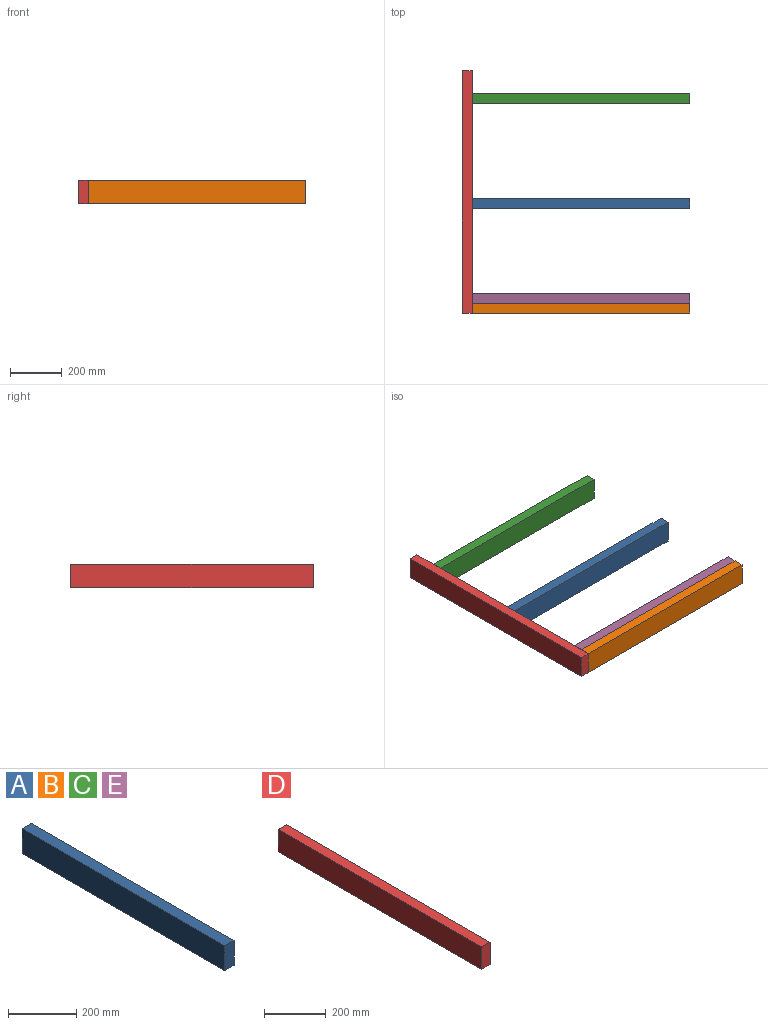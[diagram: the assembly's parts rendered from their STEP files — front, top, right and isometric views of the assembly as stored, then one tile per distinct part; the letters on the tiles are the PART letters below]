
ASSEMBLY  parts=5 mates=1
PART A: 6 faces, bbox 38.1x838.2x88.9 mm
  f0: plane 838.2x38.1mm, normal (0,0,-1), area 31935.4mm2, adj f1,f3,f4,f5
  f1: plane 838.2x88.9mm, normal (1,0,0), area 74516mm2, adj f0,f2,f4,f5
  f2: plane 838.2x38.1mm, normal (0,0,1), area 31935.4mm2, adj f1,f3,f4,f5
  f3: plane 838.2x88.9mm, normal (-1,0,0), area 74516mm2, adj f0,f2,f4,f5
  f4: plane 88.9x38.1mm, normal (0,-1,0), area 3387.1mm2, adj f0,f1,f2,f3
  f5: plane 88.9x38.1mm, normal (0,1,0), area 3387.1mm2, adj f0,f1,f2,f3
PART B: same geometry as A
PART C: same geometry as A
PART D: 6 faces, bbox 38.1x933.5x88.9 mm
  f0: plane 933.45x38.1mm, normal (0,0,-1), area 35564.4mm2, adj f1,f3,f4,f5
  f1: plane 933.45x88.9mm, normal (1,0,0), area 82983.7mm2, adj f0,f2,f4,f5
  f2: plane 933.45x38.1mm, normal (0,0,1), area 35564.4mm2, adj f1,f3,f4,f5
  f3: plane 933.45x88.9mm, normal (-1,0,0), area 82983.7mm2, adj f0,f2,f4,f5
  f4: plane 88.9x38.1mm, normal (0,-1,0), area 3387.1mm2, adj f0,f1,f2,f3
  f5: plane 88.9x38.1mm, normal (0,1,0), area 3387.1mm2, adj f0,f1,f2,f3
PART E: same geometry as A
PLACE A rot(axis=(0,0,1),90deg) t=(-1073.7,60.77,239.51)mm
PLACE B rot(axis=(0,0,1),90deg) t=(-1073.7,-342.46,239.51)mm
PLACE C rot(axis=(0,0,1),90deg) t=(-1073.7,463.99,239.51)mm
PLACE D rot(axis=(0,0,-1),180deg) t=(-1092.75,-361.51,239.51)mm
PLACE E rot(axis=(0,0,1),90deg) t=(-1073.7,-304.36,239.51)mm
MATE fastened C.f5 <-> D.f3  axis (-1,0,0) through (-1073.7,483.04,195.06)mm
